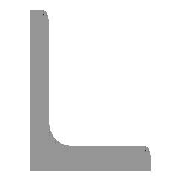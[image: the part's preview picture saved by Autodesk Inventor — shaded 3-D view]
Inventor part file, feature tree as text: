
AUTODESK INVENTOR PART (.ipt)
format: ipt  version: 2016 (Build 200138000, 138)  size: 126,976 bytes
history: native  units: mm (DEFAULTED — no unit token found)
features: other x4, sketch x3, extrude x2, plane x2
ambient origin geometry x8: Origin, YZ Plane, XZ Plane, XY Plane, X Axis, Y Axis, Z Axis, Center Point
bodies: Solid1 (feature_tree)
feature tree (11):
  parser-record x1  (decoder bookkeeping rows leaked as tree rows — omitted from the tree; the rows remain in map.json)
  other  "Driven Length"
  other  "Plano inicial"
  other  "Plano final"
  extrude  "Cuerpo"  Depth=38.1mm
  sketch  "Boceto5"  dims[d4=2400.0mm d5=0.0mm d10=0.0mm d11=0.0mm d12=-0.0mm d13=2400.0mm d14=4.826mm d15=2.286mm d16=90.0deg d17=2400.0mm d18=10.0mm d19=0.0mm]
  plane  "Plano de trabajo4"
  extrude  "Extrusión2"  Depth=4.7625mm
  sketch  "Sketch3"  dims[d0=38.1mm d1=38.1mm]
  plane  "Work Plane3"
  sketch  "Sketch4"  dims[d2=4.7625mm d3=4.7625mm]
